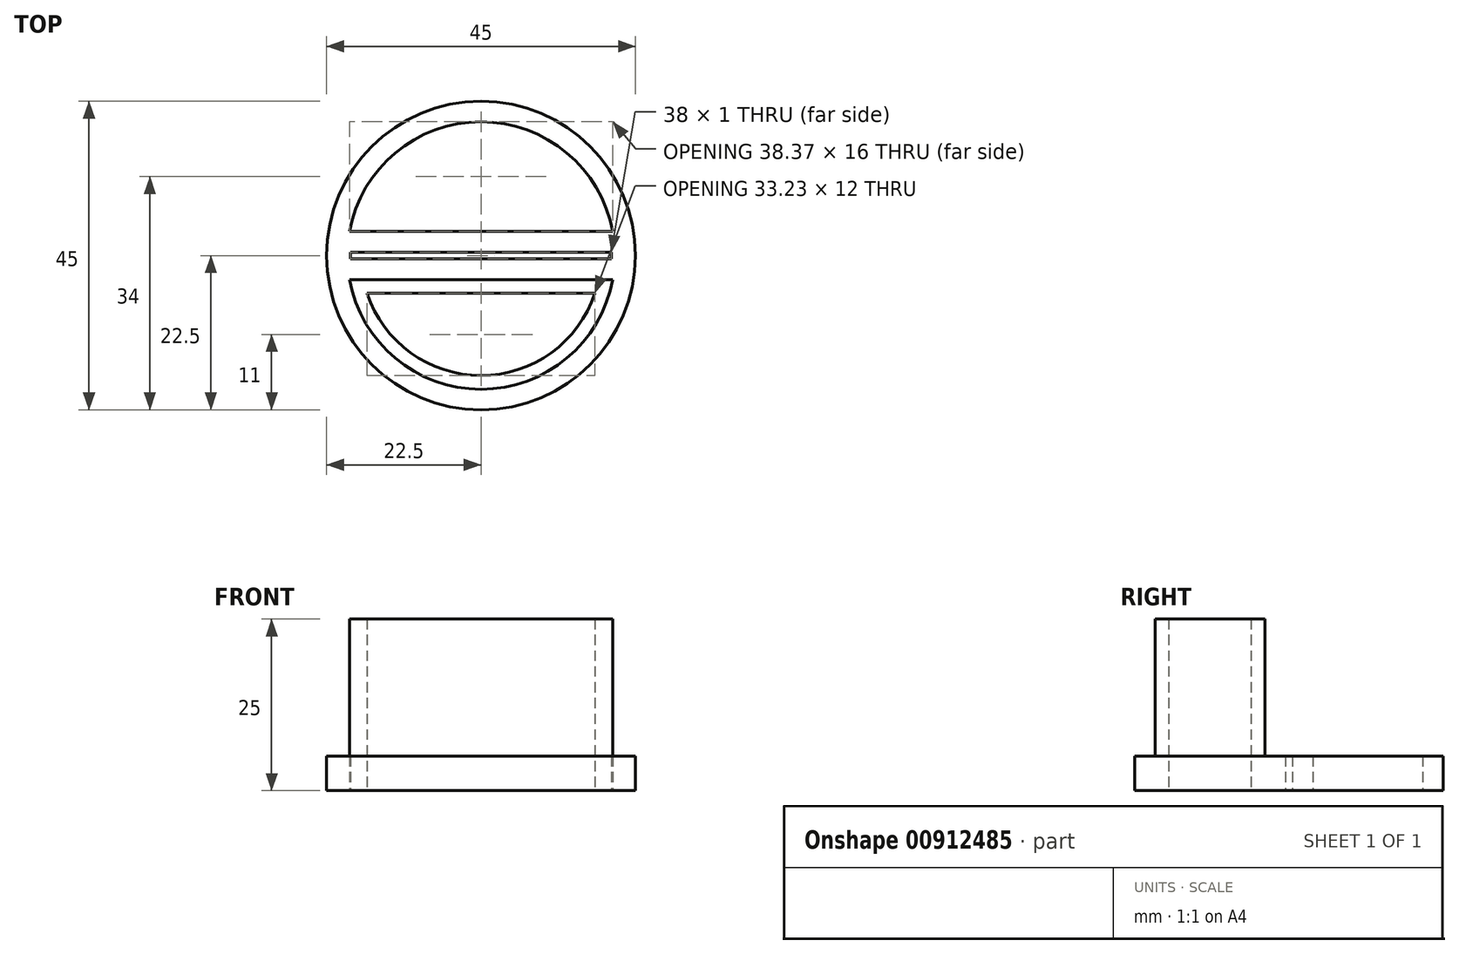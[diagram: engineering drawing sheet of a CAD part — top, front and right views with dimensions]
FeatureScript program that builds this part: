
annotation { "Feature Type Name" : "Feature", "Feature Type Description" : "" }
export const myFeature = defineFeature(function(context is Context, id is Id, definition is map)
    precondition{}
    {
        {
            var Q0;
            Q0=qCreatedBy(makeId("Top.planeOp"),FACE);
            var sketch = newSketch(context, id + "F0", { "sketchPlane" : qUnion([Q0])});
            skCircle(sketch, "E0", {"center": v(0, 0) * mm, "radius": 22.5 * mm});
            skLineSegment(sketch, "E1.bottom", {"start": v(-19, 0.5) * mm, "end": v(19, 0.5) * mm});
            skLineSegment(sketch, "E1.top", {"start": v(-19, -0.5) * mm, "end": v(19, -0.5) * mm});
            skLineSegment(sketch, "E1.left", {"start": v(-19, 0.5) * mm, "end": v(-19, -0.5) * mm});
            skLineSegment(sketch, "E1.right", {"start": v(19, 0.5) * mm, "end": v(19, -0.5) * mm});
            skPoint(sketch, "E2", {"position": v(19, 0) * mm});
            skPoint(sketch, "E3", {"position": v(0, 0.5) * mm});
            skArc(sketch, "E4", {"start": v(-19.18, 3.5) * mm, "mid": v(0, 19.5) * mm, "end": v(19.18, 3.5) * mm});
            skLineSegment(sketch, "E5", {"start": v(-19.18, 3.5) * mm, "end": v(19.18, 3.5) * mm});
            skArc(sketch, "E6", {"start": v(-19.18, -3.5) * mm, "mid": v(0, -19.5) * mm, "end": v(19.18, -3.5) * mm});
            skLineSegment(sketch, "E7", {"start": v(-19.18, -3.5) * mm, "end": v(19.18, -3.5) * mm});
            skLineSegment(sketch, "E8.0", {"start": v(-16.61, -5.5) * mm, "end": v(16.61, -5.5) * mm});
            skArc(sketch, "E8.1", {"start": v(-16.61, -5.5) * mm, "mid": v(0, -17.5) * mm, "end": v(16.61, -5.5) * mm});
            skSolve(sketch);
        }
        {
            var Q0;
            Q0 = qSketchRegion(id + "F0", true);
            extrude(context, id + "F1", {"entities" : qUnion([Q0]), "depth" : 5 * mm, "offsetDistance" : 25 * mm});
        }
        {
            var Q0;
            Q0=makeQuery(id+"F0.imprint","IMPRINT",FACE,{"disambiguationData":[TD([[makeQuery(id+"F0.imprint","IMPRINT",EDGE,{"derivedFrom":sQuery(id+"F0.wireOp",EDGE,"E6")}),1.0]])]});
            extrude(context, id + "F2", {"entities" : qUnion([Q0]), "operationType" : NewBodyOperationType.ADD, "depth" : 25 * mm, "offsetDistance" : 25 * mm});
        }
    });
